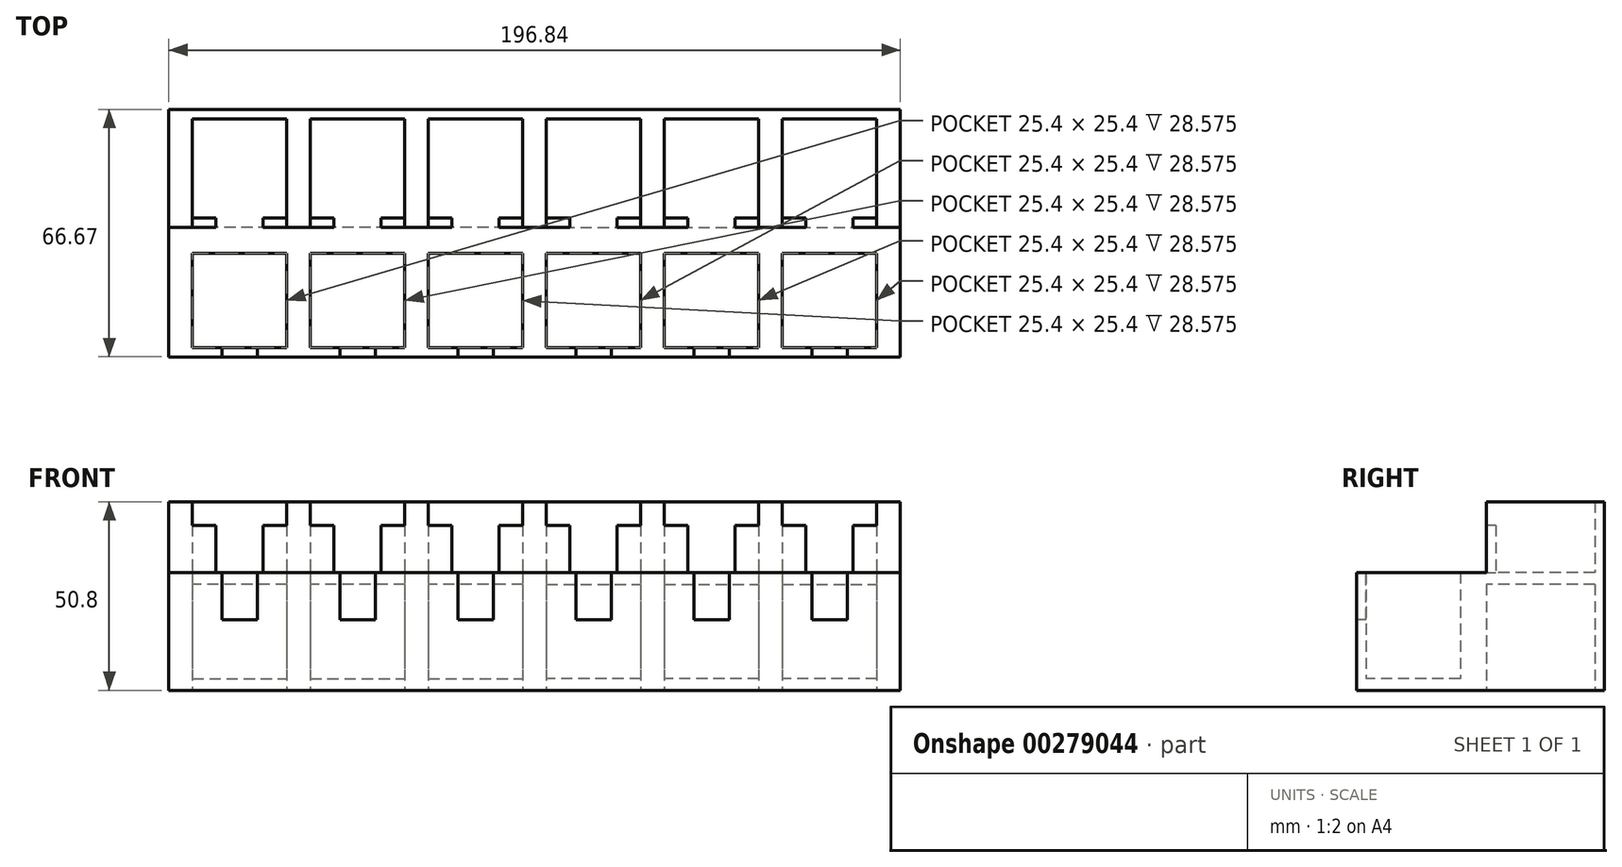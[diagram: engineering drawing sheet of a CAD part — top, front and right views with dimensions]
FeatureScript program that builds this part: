
annotation { "Feature Type Name" : "Feature", "Feature Type Description" : "" }
export const myFeature = defineFeature(function(context is Context, id is Id, definition is map)
    precondition{}
    {
        {
            var Q0;
            Q0=qCreatedBy(makeId("Right.planeOp"),FACE);
            var sketch = newSketch(context, id + "F0", { "sketchPlane" : qUnion([Q0])});
            skLineSegment(sketch, "E0", {"start": v(0, 0) * mm, "end": v(-66.67, 0) * mm});
            skLineSegment(sketch, "E1", {"start": v(-66.67, 0) * mm, "end": v(-66.68, 31.75) * mm});
            skLineSegment(sketch, "E2", {"start": v(-66.68, 31.75) * mm, "end": v(-31.75, 31.75) * mm});
            skLineSegment(sketch, "E3", {"start": v(-31.75, 31.75) * mm, "end": v(-31.75, 50.8) * mm});
            skLineSegment(sketch, "E4", {"start": v(-31.75, 50.8) * mm, "end": v(0, 50.8) * mm});
            skLineSegment(sketch, "E5", {"start": v(0, 50.8) * mm, "end": v(0, 0) * mm});
            skSolve(sketch);
        }
        {
            var Q0;
            Q0 = qSketchRegion(id + "F0", true);
            extrude(context, id + "F1", {"entities" : qUnion([Q0]), "endBound" : BoundingType.SYMMETRIC, "depth" : 196.85 * mm});
        }
        {
            var Q0;
            Q0=makeQuery(id+"F1.opExtrude","SWEPT_FACE",FACE,{"disambiguationData":[OSD([sQuery(id+"F0.wireOp",EDGE,"E0")])]});
            var sketch = newSketch(context, id + "F2", { "sketchPlane" : qUnion([Q0])});
            skLineSegment(sketch, "E6.bottom", {"start": v(-3.18, 64.13) * mm, "end": v(-28.58, 64.13) * mm});
            skLineSegment(sketch, "E6.top", {"start": v(-3.18, 38.73) * mm, "end": v(-28.58, 38.73) * mm});
            skLineSegment(sketch, "E6.left", {"start": v(-3.18, 64.13) * mm, "end": v(-3.18, 38.73) * mm});
            skLineSegment(sketch, "E6.right", {"start": v(-28.58, 64.13) * mm, "end": v(-28.58, 38.73) * mm});
            skLineSegment(sketch, "E7.bottom", {"start": v(-3.18, 31.75) * mm, "end": v(-28.58, 31.75) * mm});
            skLineSegment(sketch, "E7.top", {"start": v(-3.18, 2.54) * mm, "end": v(-28.58, 2.54) * mm});
            skLineSegment(sketch, "E7.left", {"start": v(-3.18, 31.75) * mm, "end": v(-3.18, 2.54) * mm});
            skLineSegment(sketch, "E7.right", {"start": v(-28.58, 31.75) * mm, "end": v(-28.58, 2.54) * mm});
            skLineSegment(sketch, "E8.1.0.0", {"start": v(-34.92, 2.54) * mm, "end": v(-60.33, 2.54) * mm});
            skLineSegment(sketch, "E8.1.0.1", {"start": v(-34.93, 31.75) * mm, "end": v(-34.92, 2.54) * mm});
            skLineSegment(sketch, "E8.1.0.2", {"start": v(-60.33, 31.75) * mm, "end": v(-60.33, 2.54) * mm});
            skLineSegment(sketch, "E8.1.0.3", {"start": v(-34.93, 31.75) * mm, "end": v(-60.33, 31.75) * mm});
            skLineSegment(sketch, "E8.1.0.4", {"start": v(-34.93, 64.13) * mm, "end": v(-34.93, 38.73) * mm});
            skLineSegment(sketch, "E8.1.0.5", {"start": v(-34.93, 38.73) * mm, "end": v(-60.33, 38.73) * mm});
            skLineSegment(sketch, "E8.1.0.6", {"start": v(-60.33, 64.13) * mm, "end": v(-60.33, 38.73) * mm});
            skLineSegment(sketch, "E8.1.0.7", {"start": v(-34.93, 64.13) * mm, "end": v(-60.33, 64.13) * mm});
            skLineSegment(sketch, "E8.2.0.0", {"start": v(-66.67, 2.54) * mm, "end": v(-92.08, 2.54) * mm});
            skLineSegment(sketch, "E8.2.0.1", {"start": v(-66.68, 31.75) * mm, "end": v(-66.67, 2.54) * mm});
            skLineSegment(sketch, "E8.2.0.2", {"start": v(-92.08, 31.75) * mm, "end": v(-92.08, 2.54) * mm});
            skLineSegment(sketch, "E8.2.0.3", {"start": v(-66.68, 31.75) * mm, "end": v(-92.08, 31.75) * mm});
            skLineSegment(sketch, "E8.2.0.4", {"start": v(-66.68, 64.13) * mm, "end": v(-66.68, 38.73) * mm});
            skLineSegment(sketch, "E8.2.0.5", {"start": v(-66.68, 38.73) * mm, "end": v(-92.08, 38.73) * mm});
            skLineSegment(sketch, "E8.2.0.6", {"start": v(-92.08, 64.13) * mm, "end": v(-92.08, 38.73) * mm});
            skLineSegment(sketch, "E8.2.0.7", {"start": v(-66.68, 64.13) * mm, "end": v(-92.08, 64.13) * mm});
            skLineSegment(sketch, "E8.direction1", {"start": v(-28.58, 2.54) * mm, "end": v(-60.33, 2.54) * mm, "construction": true});
            skLineSegment(sketch, "E9", {"start": v(0, 0) * mm, "end": v(0, 66.67) * mm, "construction": true});
            skLineSegment(sketch, "E10.MirrorCS", {"start": v(34.92, 2.54) * mm, "end": v(60.33, 2.54) * mm});
            skLineSegment(sketch, "E11.MirrorCS", {"start": v(3.18, 38.73) * mm, "end": v(28.58, 38.73) * mm});
            skLineSegment(sketch, "E12.MirrorCS", {"start": v(3.17, 64.13) * mm, "end": v(3.17, 38.73) * mm});
            skLineSegment(sketch, "E13.MirrorCS", {"start": v(66.67, 2.54) * mm, "end": v(92.08, 2.54) * mm});
            skLineSegment(sketch, "E14.MirrorCS", {"start": v(34.93, 64.13) * mm, "end": v(60.33, 64.13) * mm});
            skLineSegment(sketch, "E15.MirrorCS", {"start": v(92.08, 31.75) * mm, "end": v(92.08, 2.54) * mm});
            skLineSegment(sketch, "E16.MirrorCS", {"start": v(60.32, 64.13) * mm, "end": v(60.32, 38.73) * mm});
            skLineSegment(sketch, "E17.MirrorCS", {"start": v(34.93, 38.73) * mm, "end": v(60.33, 38.73) * mm});
            skLineSegment(sketch, "E18.MirrorCS", {"start": v(66.68, 64.13) * mm, "end": v(66.68, 38.73) * mm});
            skLineSegment(sketch, "E19.MirrorCS", {"start": v(92.08, 64.13) * mm, "end": v(92.08, 38.73) * mm});
            skLineSegment(sketch, "E20.MirrorCS", {"start": v(66.68, 64.13) * mm, "end": v(92.08, 64.13) * mm});
            skLineSegment(sketch, "E21.MirrorCS", {"start": v(66.68, 31.75) * mm, "end": v(66.68, 2.54) * mm});
            skLineSegment(sketch, "E22.MirrorCS", {"start": v(66.68, 31.75) * mm, "end": v(92.08, 31.75) * mm});
            skLineSegment(sketch, "E23.MirrorCS", {"start": v(66.68, 38.73) * mm, "end": v(92.08, 38.73) * mm});
            skLineSegment(sketch, "E24.MirrorCS", {"start": v(3.18, 64.13) * mm, "end": v(28.58, 64.13) * mm});
            skLineSegment(sketch, "E25.MirrorCS", {"start": v(34.93, 64.13) * mm, "end": v(34.93, 38.73) * mm});
            skLineSegment(sketch, "E26.MirrorCS", {"start": v(34.93, 31.75) * mm, "end": v(60.33, 31.75) * mm});
            skLineSegment(sketch, "E27.MirrorCS", {"start": v(28.57, 64.13) * mm, "end": v(28.58, 38.73) * mm});
            skLineSegment(sketch, "E28.MirrorCS", {"start": v(3.18, 31.75) * mm, "end": v(28.58, 31.75) * mm});
            skLineSegment(sketch, "E29.MirrorCS", {"start": v(3.18, 2.54) * mm, "end": v(28.58, 2.54) * mm});
            skLineSegment(sketch, "E30.MirrorCS", {"start": v(3.17, 31.75) * mm, "end": v(3.17, 2.54) * mm});
            skLineSegment(sketch, "E31.MirrorCS", {"start": v(28.57, 31.75) * mm, "end": v(28.58, 2.54) * mm});
            skLineSegment(sketch, "E32.MirrorCS", {"start": v(34.93, 31.75) * mm, "end": v(34.93, 2.54) * mm});
            skLineSegment(sketch, "E33.MirrorCS", {"start": v(60.33, 31.75) * mm, "end": v(60.33, 2.54) * mm});
            skSolve(sketch);
        }
        {
            var Q0;
            Q0 = qSketchRegion(id + "F2", true);
            extrude(context, id + "F3", {"entities" : qUnion([Q0]), "operationType" : NewBodyOperationType.REMOVE, "endBound" : BoundingType.THROUGH_ALL, "oppositeDirection" : true, "depth" : 25.4 * mm});
        }
        {
            var Q0;
            Q0=makeQuery(id+"F1.opExtrude","SWEPT_FACE",FACE,{"disambiguationData":[OSD([sQuery(id+"F0.wireOp",EDGE,"E2")])]});
            var sketch = newSketch(context, id + "F4", { "sketchPlane" : qUnion([Q0])});
            skLineSegment(sketch, "E34.bottom", {"start": v(-92.08, -2.54) * mm, "end": v(-66.68, -2.54) * mm});
            skLineSegment(sketch, "E34.top", {"start": v(-92.08, -31.75) * mm, "end": v(-66.68, -31.75) * mm});
            skLineSegment(sketch, "E34.left", {"start": v(-92.08, -2.54) * mm, "end": v(-92.08, -31.75) * mm});
            skLineSegment(sketch, "E34.right", {"start": v(-66.68, -2.54) * mm, "end": v(-66.68, -31.75) * mm});
            skLineSegment(sketch, "E35.bottom", {"start": v(-60.33, -2.54) * mm, "end": v(-34.93, -2.54) * mm});
            skLineSegment(sketch, "E35.top", {"start": v(-60.33, -31.75) * mm, "end": v(-34.93, -31.75) * mm});
            skLineSegment(sketch, "E35.left", {"start": v(-60.33, -2.54) * mm, "end": v(-60.33, -31.75) * mm});
            skLineSegment(sketch, "E35.right", {"start": v(-34.93, -2.54) * mm, "end": v(-34.93, -31.75) * mm});
            skLineSegment(sketch, "E36.bottom", {"start": v(-28.58, -2.54) * mm, "end": v(-3.18, -2.54) * mm});
            skLineSegment(sketch, "E36.top", {"start": v(-28.57, -31.75) * mm, "end": v(-3.18, -31.75) * mm});
            skLineSegment(sketch, "E36.left", {"start": v(-28.58, -2.54) * mm, "end": v(-28.58, -31.75) * mm});
            skLineSegment(sketch, "E36.right", {"start": v(-3.18, -2.54) * mm, "end": v(-3.18, -31.75) * mm});
            skLineSegment(sketch, "E37.bottom", {"start": v(3.17, -2.54) * mm, "end": v(28.58, -2.54) * mm});
            skLineSegment(sketch, "E37.top", {"start": v(3.17, -31.75) * mm, "end": v(28.58, -31.75) * mm});
            skLineSegment(sketch, "E37.left", {"start": v(3.17, -2.54) * mm, "end": v(3.17, -31.75) * mm});
            skLineSegment(sketch, "E37.right", {"start": v(28.57, -2.54) * mm, "end": v(28.57, -31.75) * mm});
            skLineSegment(sketch, "E38.bottom", {"start": v(34.92, -2.54) * mm, "end": v(60.32, -2.54) * mm});
            skLineSegment(sketch, "E38.top", {"start": v(34.92, -31.75) * mm, "end": v(60.33, -31.75) * mm});
            skLineSegment(sketch, "E38.left", {"start": v(34.92, -2.54) * mm, "end": v(34.92, -31.75) * mm});
            skLineSegment(sketch, "E38.right", {"start": v(60.33, -2.54) * mm, "end": v(60.33, -31.75) * mm});
            skLineSegment(sketch, "E39.bottom", {"start": v(66.67, -2.54) * mm, "end": v(92.08, -2.54) * mm});
            skLineSegment(sketch, "E39.top", {"start": v(66.67, -31.75) * mm, "end": v(92.08, -31.75) * mm});
            skLineSegment(sketch, "E39.left", {"start": v(66.67, -2.54) * mm, "end": v(66.67, -31.75) * mm});
            skLineSegment(sketch, "E39.right", {"start": v(92.08, -2.54) * mm, "end": v(92.08, -31.75) * mm});
            skSolve(sketch);
        }
        {
            var Q0;
            {var subQ7=sQuery(id+"F4.wireOp",EDGE,"E37.bottom");Q0=makeQuery(id+"F4.imprint","IMPRINT",FACE,{"disambiguationData":[TD([[makeQuery(id+"F4.imprint","IMPRINT",EDGE,{"derivedFrom":subQ7}),-1.0]])]});}
            var Q1;
            {var subQ7=sQuery(id+"F4.wireOp",EDGE,"E38.bottom");Q1=makeQuery(id+"F4.imprint","IMPRINT",FACE,{"disambiguationData":[TD([[makeQuery(id+"F4.imprint","IMPRINT",EDGE,{"derivedFrom":subQ7}),-1.0]])]});}
            var Q2;
            {var subQ7=sQuery(id+"F4.wireOp",EDGE,"E39.bottom");Q2=makeQuery(id+"F4.imprint","IMPRINT",FACE,{"disambiguationData":[TD([[makeQuery(id+"F4.imprint","IMPRINT",EDGE,{"derivedFrom":subQ7}),-1.0]])]});}
            var Q3;
            {var subQ7=sQuery(id+"F4.wireOp",EDGE,"E36.bottom");Q3=makeQuery(id+"F4.imprint","IMPRINT",FACE,{"disambiguationData":[TD([[makeQuery(id+"F4.imprint","IMPRINT",EDGE,{"derivedFrom":subQ7}),-1.0]])]});}
            var Q4;
            {var subQ7=sQuery(id+"F4.wireOp",EDGE,"E34.bottom");Q4=makeQuery(id+"F4.imprint","IMPRINT",FACE,{"disambiguationData":[TD([[makeQuery(id+"F4.imprint","IMPRINT",EDGE,{"derivedFrom":subQ7}),-1.0]])]});}
            var Q5;
            {var subQ7=sQuery(id+"F4.wireOp",EDGE,"E35.bottom");Q5=makeQuery(id+"F4.imprint","IMPRINT",FACE,{"disambiguationData":[TD([[makeQuery(id+"F4.imprint","IMPRINT",EDGE,{"derivedFrom":subQ7}),-1.0]])]});}
            extrude(context, id + "F5", {"entities" : qUnion([Q0, Q1, Q2, Q3, Q4, Q5]), "operationType" : NewBodyOperationType.ADD, "oppositeDirection" : true, "depth" : 3.17 * mm});
        }
        {
            var Q0;
            Q0=makeQuery(id+"F5.boolean.opBoolean","MERGE",FACE,{"derivedFrom":[makeQuery(id+"F1.opExtrude","SWEPT_FACE",FACE,{"disambiguationData":[OSD([sQuery(id+"F0.wireOp",EDGE,"E2")])]}),makeQuery(id+"F5.opExtrude","CAP_FACE",FACE,{"disambiguationData":[OSD([sQuery(id+"F4.wireOp",EDGE,"E34.bottom"),sQuery(id+"F4.wireOp",EDGE,"E34.top"),sQuery(id+"F4.wireOp",EDGE,"E34.left"),sQuery(id+"F4.wireOp",EDGE,"E34.right")])],"isStart":true}),makeQuery(id+"F5.opExtrude","CAP_FACE",FACE,{"disambiguationData":[OSD([sQuery(id+"F4.wireOp",EDGE,"E35.bottom"),sQuery(id+"F4.wireOp",EDGE,"E35.top"),sQuery(id+"F4.wireOp",EDGE,"E35.left"),sQuery(id+"F4.wireOp",EDGE,"E35.right")])],"isStart":true}),makeQuery(id+"F5.opExtrude","CAP_FACE",FACE,{"disambiguationData":[OSD([sQuery(id+"F4.wireOp",EDGE,"E36.bottom"),sQuery(id+"F4.wireOp",EDGE,"E36.top"),sQuery(id+"F4.wireOp",EDGE,"E36.left"),sQuery(id+"F4.wireOp",EDGE,"E36.right")])],"isStart":true}),makeQuery(id+"F5.opExtrude","CAP_FACE",FACE,{"disambiguationData":[OSD([sQuery(id+"F4.wireOp",EDGE,"E37.bottom"),sQuery(id+"F4.wireOp",EDGE,"E37.top"),sQuery(id+"F4.wireOp",EDGE,"E37.left"),sQuery(id+"F4.wireOp",EDGE,"E37.right")])],"isStart":true}),makeQuery(id+"F5.opExtrude","CAP_FACE",FACE,{"disambiguationData":[OSD([sQuery(id+"F4.wireOp",EDGE,"E38.bottom"),sQuery(id+"F4.wireOp",EDGE,"E38.top"),sQuery(id+"F4.wireOp",EDGE,"E38.left"),sQuery(id+"F4.wireOp",EDGE,"E38.right")])],"isStart":true}),makeQuery(id+"F5.opExtrude","CAP_FACE",FACE,{"disambiguationData":[OSD([sQuery(id+"F4.wireOp",EDGE,"E39.bottom"),sQuery(id+"F4.wireOp",EDGE,"E39.top"),sQuery(id+"F4.wireOp",EDGE,"E39.left"),sQuery(id+"F4.wireOp",EDGE,"E39.right")])],"isStart":true})]});
            var sketch = newSketch(context, id + "F6", { "sketchPlane" : qUnion([Q0])});
            skLineSegment(sketch, "E40.bottom", {"start": v(-92.08, -31.75) * mm, "end": v(-85.73, -31.75) * mm});
            skLineSegment(sketch, "E40.top", {"start": v(-92.08, -29.2) * mm, "end": v(-85.73, -29.2) * mm});
            skLineSegment(sketch, "E40.left", {"start": v(-92.08, -31.75) * mm, "end": v(-92.08, -29.2) * mm});
            skLineSegment(sketch, "E40.right", {"start": v(-85.73, -31.75) * mm, "end": v(-85.73, -29.2) * mm});
            skLineSegment(sketch, "E41", {"start": v(-79.38, -2.54) * mm, "end": v(-79.38, -25.06) * mm, "construction": true});
            skLineSegment(sketch, "E42.MirrorCS", {"start": v(-66.67, -31.75) * mm, "end": v(-66.67, -29.2) * mm});
            skLineSegment(sketch, "E43.MirrorCS", {"start": v(-66.67, -29.2) * mm, "end": v(-73.02, -29.2) * mm});
            skLineSegment(sketch, "E44.MirrorCS", {"start": v(-66.67, -31.75) * mm, "end": v(-73.02, -31.75) * mm});
            skLineSegment(sketch, "E45.MirrorCS", {"start": v(-73.02, -31.75) * mm, "end": v(-73.02, -29.2) * mm});
            skLineSegment(sketch, "E46.1.0.0", {"start": v(-41.27, -31.75) * mm, "end": v(-41.27, -29.2) * mm});
            skLineSegment(sketch, "E46.1.0.1", {"start": v(-34.92, -31.75) * mm, "end": v(-41.27, -31.75) * mm});
            skLineSegment(sketch, "E46.1.0.2", {"start": v(-34.92, -29.2) * mm, "end": v(-41.27, -29.2) * mm});
            skLineSegment(sketch, "E46.1.0.3", {"start": v(-34.92, -31.75) * mm, "end": v(-34.92, -29.2) * mm});
            skLineSegment(sketch, "E46.1.0.4", {"start": v(-53.98, -31.75) * mm, "end": v(-53.98, -29.2) * mm});
            skLineSegment(sketch, "E46.1.0.5", {"start": v(-60.33, -31.75) * mm, "end": v(-60.33, -29.2) * mm});
            skLineSegment(sketch, "E46.1.0.6", {"start": v(-60.33, -31.75) * mm, "end": v(-53.98, -31.75) * mm});
            skLineSegment(sketch, "E46.1.0.7", {"start": v(-60.33, -29.2) * mm, "end": v(-53.98, -29.2) * mm});
            skLineSegment(sketch, "E46.2.0.0", {"start": v(-9.52, -31.75) * mm, "end": v(-9.52, -29.2) * mm});
            skLineSegment(sketch, "E46.2.0.1", {"start": v(-3.17, -31.75) * mm, "end": v(-9.52, -31.75) * mm});
            skLineSegment(sketch, "E46.2.0.2", {"start": v(-3.17, -29.2) * mm, "end": v(-9.52, -29.2) * mm});
            skLineSegment(sketch, "E46.2.0.3", {"start": v(-3.17, -31.75) * mm, "end": v(-3.17, -29.2) * mm});
            skLineSegment(sketch, "E46.2.0.4", {"start": v(-22.23, -31.75) * mm, "end": v(-22.23, -29.2) * mm});
            skLineSegment(sketch, "E46.2.0.5", {"start": v(-28.58, -31.75) * mm, "end": v(-28.58, -29.2) * mm});
            skLineSegment(sketch, "E46.2.0.6", {"start": v(-28.58, -31.75) * mm, "end": v(-22.23, -31.75) * mm});
            skLineSegment(sketch, "E46.2.0.7", {"start": v(-28.58, -29.2) * mm, "end": v(-22.23, -29.2) * mm});
            skLineSegment(sketch, "E46.3.0.0", {"start": v(22.23, -31.75) * mm, "end": v(22.23, -29.2) * mm});
            skLineSegment(sketch, "E46.3.0.1", {"start": v(28.58, -31.75) * mm, "end": v(22.23, -31.75) * mm});
            skLineSegment(sketch, "E46.3.0.2", {"start": v(28.58, -29.2) * mm, "end": v(22.23, -29.2) * mm});
            skLineSegment(sketch, "E46.3.0.3", {"start": v(28.58, -31.75) * mm, "end": v(28.58, -29.2) * mm});
            skLineSegment(sketch, "E46.3.0.4", {"start": v(9.52, -31.75) * mm, "end": v(9.52, -29.2) * mm});
            skLineSegment(sketch, "E46.3.0.5", {"start": v(3.17, -31.75) * mm, "end": v(3.17, -29.2) * mm});
            skLineSegment(sketch, "E46.3.0.6", {"start": v(3.17, -31.75) * mm, "end": v(9.52, -31.75) * mm});
            skLineSegment(sketch, "E46.3.0.7", {"start": v(3.17, -29.2) * mm, "end": v(9.52, -29.2) * mm});
            skLineSegment(sketch, "E46.4.0.0", {"start": v(53.98, -31.75) * mm, "end": v(53.98, -29.2) * mm});
            skLineSegment(sketch, "E46.4.0.1", {"start": v(60.33, -31.75) * mm, "end": v(53.98, -31.75) * mm});
            skLineSegment(sketch, "E46.4.0.2", {"start": v(60.33, -29.2) * mm, "end": v(53.98, -29.2) * mm});
            skLineSegment(sketch, "E46.4.0.3", {"start": v(60.33, -31.75) * mm, "end": v(60.33, -29.2) * mm});
            skLineSegment(sketch, "E46.4.0.4", {"start": v(41.27, -31.75) * mm, "end": v(41.27, -29.2) * mm});
            skLineSegment(sketch, "E46.4.0.5", {"start": v(34.92, -31.75) * mm, "end": v(34.92, -29.2) * mm});
            skLineSegment(sketch, "E46.4.0.6", {"start": v(34.92, -31.75) * mm, "end": v(41.27, -31.75) * mm});
            skLineSegment(sketch, "E46.4.0.7", {"start": v(34.92, -29.2) * mm, "end": v(41.27, -29.2) * mm});
            skLineSegment(sketch, "E46.5.0.0", {"start": v(85.73, -31.75) * mm, "end": v(85.73, -29.2) * mm});
            skLineSegment(sketch, "E46.5.0.1", {"start": v(92.08, -31.75) * mm, "end": v(85.73, -31.75) * mm});
            skLineSegment(sketch, "E46.5.0.2", {"start": v(92.08, -29.2) * mm, "end": v(85.73, -29.2) * mm});
            skLineSegment(sketch, "E46.5.0.3", {"start": v(92.08, -31.75) * mm, "end": v(92.08, -29.2) * mm});
            skLineSegment(sketch, "E46.5.0.4", {"start": v(73.02, -31.75) * mm, "end": v(73.02, -29.2) * mm});
            skLineSegment(sketch, "E46.5.0.5", {"start": v(66.67, -31.75) * mm, "end": v(66.67, -29.2) * mm});
            skLineSegment(sketch, "E46.5.0.6", {"start": v(66.67, -31.75) * mm, "end": v(73.02, -31.75) * mm});
            skLineSegment(sketch, "E46.5.0.7", {"start": v(66.67, -29.2) * mm, "end": v(73.02, -29.2) * mm});
            skLineSegment(sketch, "E46.direction1", {"start": v(-92.08, -31.75) * mm, "end": v(-60.33, -31.75) * mm, "construction": true});
            skSolve(sketch);
        }
        {
            var Q0;
            Q0 = qSketchRegion(id + "F6", true);
            extrude(context, id + "F7", {"entities" : qUnion([Q0]), "operationType" : NewBodyOperationType.ADD, "depth" : 12.7 * mm});
        }
        {
            var Q0;
            Q0=makeQuery(id+"F5.boolean.opBoolean","MERGE",FACE,{"derivedFrom":[makeQuery(id+"F1.opExtrude","SWEPT_FACE",FACE,{"disambiguationData":[OSD([sQuery(id+"F0.wireOp",EDGE,"E2")])]}),makeQuery(id+"F5.opExtrude","CAP_FACE",FACE,{"disambiguationData":[OSD([sQuery(id+"F4.wireOp",EDGE,"E34.bottom"),sQuery(id+"F4.wireOp",EDGE,"E34.top"),sQuery(id+"F4.wireOp",EDGE,"E34.left"),sQuery(id+"F4.wireOp",EDGE,"E34.right")])],"isStart":true}),makeQuery(id+"F5.opExtrude","CAP_FACE",FACE,{"disambiguationData":[OSD([sQuery(id+"F4.wireOp",EDGE,"E35.bottom"),sQuery(id+"F4.wireOp",EDGE,"E35.top"),sQuery(id+"F4.wireOp",EDGE,"E35.left"),sQuery(id+"F4.wireOp",EDGE,"E35.right")])],"isStart":true}),makeQuery(id+"F5.opExtrude","CAP_FACE",FACE,{"disambiguationData":[OSD([sQuery(id+"F4.wireOp",EDGE,"E36.bottom"),sQuery(id+"F4.wireOp",EDGE,"E36.top"),sQuery(id+"F4.wireOp",EDGE,"E36.left"),sQuery(id+"F4.wireOp",EDGE,"E36.right")])],"isStart":true}),makeQuery(id+"F5.opExtrude","CAP_FACE",FACE,{"disambiguationData":[OSD([sQuery(id+"F4.wireOp",EDGE,"E37.bottom"),sQuery(id+"F4.wireOp",EDGE,"E37.top"),sQuery(id+"F4.wireOp",EDGE,"E37.left"),sQuery(id+"F4.wireOp",EDGE,"E37.right")])],"isStart":true}),makeQuery(id+"F5.opExtrude","CAP_FACE",FACE,{"disambiguationData":[OSD([sQuery(id+"F4.wireOp",EDGE,"E38.bottom"),sQuery(id+"F4.wireOp",EDGE,"E38.top"),sQuery(id+"F4.wireOp",EDGE,"E38.left"),sQuery(id+"F4.wireOp",EDGE,"E38.right")])],"isStart":true}),makeQuery(id+"F5.opExtrude","CAP_FACE",FACE,{"disambiguationData":[OSD([sQuery(id+"F4.wireOp",EDGE,"E39.bottom"),sQuery(id+"F4.wireOp",EDGE,"E39.top"),sQuery(id+"F4.wireOp",EDGE,"E39.left"),sQuery(id+"F4.wireOp",EDGE,"E39.right")])],"isStart":true})]});
            var sketch = newSketch(context, id + "F8", { "sketchPlane" : qUnion([Q0])});
            skLineSegment(sketch, "E47.bottom", {"start": v(-84.14, -64.13) * mm, "end": v(-74.61, -64.13) * mm});
            skLineSegment(sketch, "E47.top", {"start": v(-84.14, -66.68) * mm, "end": v(-74.61, -66.68) * mm});
            skLineSegment(sketch, "E47.left", {"start": v(-84.14, -64.13) * mm, "end": v(-84.14, -66.68) * mm});
            skLineSegment(sketch, "E47.right", {"start": v(-74.61, -64.13) * mm, "end": v(-74.61, -66.68) * mm});
            skLineSegment(sketch, "E48", {"start": v(-92.08, -64.13) * mm, "end": v(-84.14, -64.13) * mm, "construction": true});
            skLineSegment(sketch, "E49", {"start": v(-66.68, -64.13) * mm, "end": v(-74.61, -64.13) * mm, "construction": true});
            skLineSegment(sketch, "E50.1.0.0", {"start": v(-52.39, -66.68) * mm, "end": v(-42.86, -66.68) * mm});
            skLineSegment(sketch, "E50.1.0.1", {"start": v(-42.86, -64.13) * mm, "end": v(-42.86, -66.68) * mm});
            skLineSegment(sketch, "E50.1.0.2", {"start": v(-52.39, -64.13) * mm, "end": v(-52.39, -66.68) * mm});
            skLineSegment(sketch, "E50.2.0.0", {"start": v(-20.64, -66.68) * mm, "end": v(-11.11, -66.68) * mm});
            skLineSegment(sketch, "E50.2.0.1", {"start": v(-11.11, -64.13) * mm, "end": v(-11.11, -66.68) * mm});
            skLineSegment(sketch, "E50.2.0.2", {"start": v(-20.64, -64.13) * mm, "end": v(-20.64, -66.68) * mm});
            skLineSegment(sketch, "E50.direction1", {"start": v(-84.14, -66.68) * mm, "end": v(-52.39, -66.68) * mm, "construction": true});
            skLineSegment(sketch, "E51.0.3.0", {"start": v(11.11, -66.68) * mm, "end": v(20.64, -66.68) * mm});
            skLineSegment(sketch, "E51.3.3.0", {"start": v(20.64, -64.13) * mm, "end": v(20.64, -66.68) * mm});
            skLineSegment(sketch, "E51.6.3.0", {"start": v(11.11, -64.13) * mm, "end": v(11.11, -66.68) * mm});
            skLineSegment(sketch, "E51.0.4.0", {"start": v(42.86, -66.68) * mm, "end": v(52.39, -66.68) * mm});
            skLineSegment(sketch, "E51.3.4.0", {"start": v(52.39, -64.13) * mm, "end": v(52.39, -66.68) * mm});
            skLineSegment(sketch, "E51.6.4.0", {"start": v(42.86, -64.13) * mm, "end": v(42.86, -66.68) * mm});
            skLineSegment(sketch, "E51.0.5.0", {"start": v(74.61, -66.68) * mm, "end": v(84.14, -66.68) * mm});
            skLineSegment(sketch, "E51.3.5.0", {"start": v(84.14, -64.13) * mm, "end": v(84.14, -66.68) * mm});
            skLineSegment(sketch, "E51.6.5.0", {"start": v(74.61, -64.13) * mm, "end": v(74.61, -66.68) * mm});
            skSolve(sketch);
        }
        {
            var Q0;
            Q0 = qSketchRegion(id + "F8", true);
            var Q1;
            Q1=makeQuery(id+"F8.imprint","IMPRINT",FACE,{"disambiguationData":[TD([[makeQuery(id+"F8.imprint","IMPRINT",EDGE,{"derivedFrom":sQuery(id+"F8.wireOp",EDGE,"E50.1.0.0")}),-1.0]])]});
            var Q2;
            Q2=makeQuery(id+"F8.imprint","IMPRINT",FACE,{"disambiguationData":[TD([[makeQuery(id+"F8.imprint","IMPRINT",EDGE,{"derivedFrom":sQuery(id+"F8.wireOp",EDGE,"E50.2.0.0")}),-1.0]])]});
            var Q3;
            Q3=makeQuery(id+"F8.imprint","IMPRINT",FACE,{"disambiguationData":[TD([[makeQuery(id+"F8.imprint","IMPRINT",EDGE,{"derivedFrom":sQuery(id+"F8.wireOp",EDGE,"E51.0.3.0")}),-1.0]])]});
            var Q4;
            Q4=makeQuery(id+"F8.imprint","IMPRINT",FACE,{"disambiguationData":[TD([[makeQuery(id+"F8.imprint","IMPRINT",EDGE,{"derivedFrom":sQuery(id+"F8.wireOp",EDGE,"E51.0.4.0")}),-1.0]])]});
            var Q5;
            Q5=makeQuery(id+"F8.imprint","IMPRINT",FACE,{"disambiguationData":[TD([[makeQuery(id+"F8.imprint","IMPRINT",EDGE,{"derivedFrom":sQuery(id+"F8.wireOp",EDGE,"E51.0.5.0")}),-1.0]])]});
            extrude(context, id + "F9", {"entities" : qUnion([Q0, Q1, Q2, Q3, Q4, Q5]), "operationType" : NewBodyOperationType.REMOVE, "oppositeDirection" : true, "depth" : 12.7 * mm});
        }
        {
            var Q0;
            Q0=makeQuery(id+"F1.opExtrude","SWEPT_FACE",FACE,{"disambiguationData":[OSD([sQuery(id+"F0.wireOp",EDGE,"E0")])]});
            var sketch = newSketch(context, id + "F10", { "sketchPlane" : qUnion([Q0])});
            skLineSegment(sketch, "E52.bottom", {"start": v(-98.43, 66.67) * mm, "end": v(92.08, 66.67) * mm});
            skLineSegment(sketch, "E52.top", {"start": v(-98.43, 38.73) * mm, "end": v(92.08, 38.73) * mm});
            skLineSegment(sketch, "E52.left", {"start": v(-98.43, 66.67) * mm, "end": v(-98.43, 38.73) * mm});
            skLineSegment(sketch, "E52.right", {"start": v(92.08, 66.67) * mm, "end": v(92.08, 38.73) * mm});
            skSolve(sketch);
        }
        {
            var Q0;
            Q0 = qSketchRegion(id + "F10", true);
            extrude(context, id + "F11", {"entities" : qUnion([Q0]), "operationType" : NewBodyOperationType.ADD, "oppositeDirection" : true, "depth" : 3.17 * mm});
        }
    });
